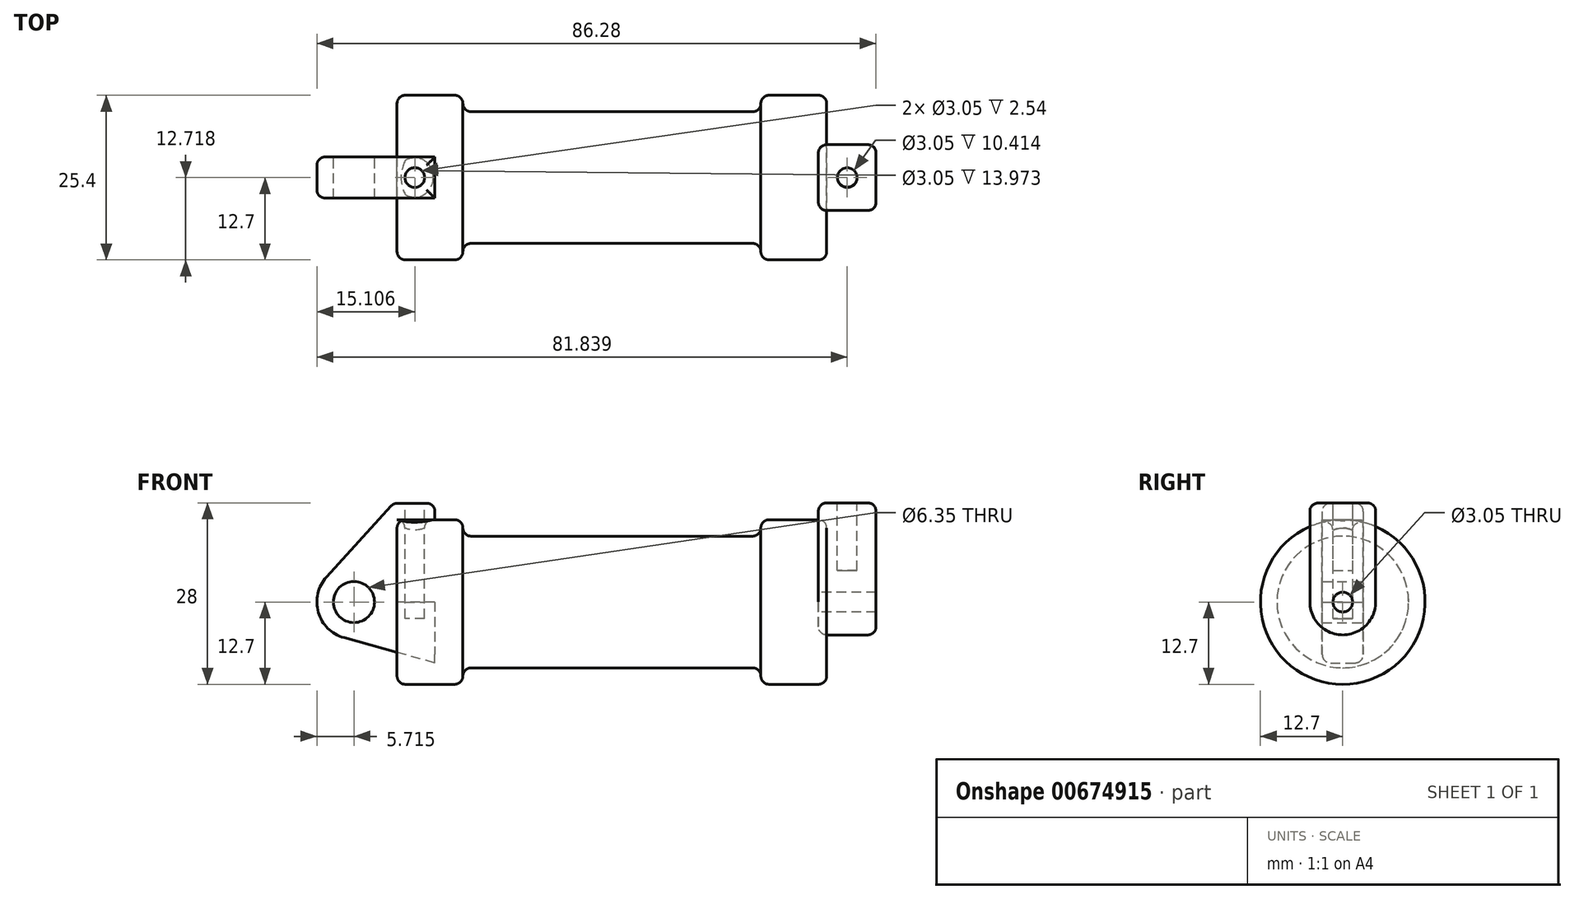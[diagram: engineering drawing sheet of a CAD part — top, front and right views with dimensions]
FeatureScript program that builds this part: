
annotation { "Feature Type Name" : "Feature", "Feature Type Description" : "" }
export const myFeature = defineFeature(function(context is Context, id is Id, definition is map)
    precondition{}
    {
        {
            var Q0;
            Q0=qCreatedBy(makeId("Front.planeOp"),FACE);
            var sketch = newSketch(context, id + "F0", { "sketchPlane" : qUnion([Q0])});
            skLineSegment(sketch, "E0", {"start": v(0, 0) * mm, "end": v(0, 12.7) * mm});
            skLineSegment(sketch, "E1", {"start": v(0, 12.7) * mm, "end": v(10.16, 12.7) * mm});
            skLineSegment(sketch, "E2", {"start": v(10.16, 12.7) * mm, "end": v(10.16, 10.16) * mm});
            skLineSegment(sketch, "E3", {"start": v(10.16, 10.16) * mm, "end": v(56.13, 10.16) * mm});
            skLineSegment(sketch, "E4", {"start": v(56.13, 10.16) * mm, "end": v(56.13, 12.7) * mm});
            skLineSegment(sketch, "E5", {"start": v(56.13, 12.7) * mm, "end": v(66.3, 12.7) * mm});
            skLineSegment(sketch, "E6", {"start": v(66.3, 12.7) * mm, "end": v(66.3, 0) * mm});
            skLineSegment(sketch, "E7", {"start": v(66.3, 0) * mm, "end": v(0, 0) * mm});
            skLineSegment(sketch, "E8", {"start": v(5.84, 15.24) * mm, "end": v(-0.5, 15.24) * mm});
            skLineSegment(sketch, "E9", {"start": v(-0.5, 15.24) * mm, "end": v(-10.88, 3.85) * mm});
            skLineSegment(sketch, "E10", {"start": v(0, 0) * mm, "end": v(-6.65, 0) * mm});
            skCircle(sketch, "E11", {"center": v(-6.65, 0) * mm, "radius": 5.72 * mm});
            skCircle(sketch, "E12", {"center": v(-6.65, 0) * mm, "radius": 3.18 * mm});
            skLineSegment(sketch, "E13", {"start": v(5.84, 15.24) * mm, "end": v(5.84, -9.4) * mm});
            skLineSegment(sketch, "E14", {"start": v(5.84, -9.4) * mm, "end": v(-8.18, -5.5) * mm});
            skSolve(sketch);
        }
        {
            var Q0;
            {var subQ0=sQuery(id+"F0.wireOp",EDGE,"E2");Q0=makeQuery(id+"F0.imprint","IMPRINT",FACE,{"disambiguationData":[TD([[makeQuery(id+"F0.imprint","IMPRINT",EDGE,{"derivedFrom":subQ0}),-1.0]])]});}
            var Q1;
            {var subQ0=sQuery(id+"F0.wireOp",EDGE,"E0");Q1=makeQuery(id+"F0.imprint","IMPRINT",FACE,{"disambiguationData":[TD([[makeQuery(id+"F0.imprint","IMPRINT",EDGE,{"derivedFrom":subQ0}),-1.0]])]});}
            var Q2;
            Q2 = qSketchRegion(id + "Fg4UrmAE8MYNZPA_2", true);
            var Q3;
            Q3=sQuery(id+"F0.wireOp",EDGE,"E7");
            revolve(context, id + "F1", {"entities" : qUnion([Q0, Q1, Q2]), "axis" : qUnion([Q3]), "revolveType" : RevolveType.FULL});
        }
        {
            var Q0;
            {var subQ1=sQuery(id+"F0.wireOp",EDGE,"E0");Q0=makeQuery(id+"F0.imprint","IMPRINT",FACE,{"disambiguationData":[TD([[makeQuery(id+"F0.imprint","IMPRINT",EDGE,{"derivedFrom":subQ1}),1.0]])]});}
            var Q1;
            {var subQ5=sQuery(id+"F0.wireOp",EDGE,"E12");Q1=makeQuery(id+"F0.imprint","IMPRINT",FACE,{"disambiguationData":[TD([[makeQuery(id+"F0.imprint","IMPRINT",EDGE,{"derivedFrom":subQ5}),-1.0]])]});}
            var Q2;
            {var subQ0=sQuery(id+"F0.wireOp",EDGE,"E14");Q2=makeQuery(id+"F0.imprint","IMPRINT",FACE,{"disambiguationData":[TD([[makeQuery(id+"F0.imprint","IMPRINT",EDGE,{"derivedFrom":subQ0}),-1.0]])]});}
            var Q3;
            Q3 = qSketchRegion(id + "Fg4UrmAE8MYNZPA_2", true);
            extrude(context, id + "F2", {"entities" : qUnion([Q0, Q1, Q2, Q3]), "endBound" : BoundingType.SYMMETRIC, "depth" : 6.35 * mm, "offsetDistance" : 25.4 * mm});
        }
        {
            var Q0;
            Q0=makeQuery(id+"F1.opRevolve","SWEPT_FACE",FACE,{"disambiguationData":[OSD([sQuery(id+"F0.wireOp",EDGE,"E6")])]});
            var sketch = newSketch(context, id + "F3", { "sketchPlane" : qUnion([Q0])});
            skCircle(sketch, "E15", {"center": v(0, 0) * mm, "radius": 5.08 * mm});
            skCircle(sketch, "E16", {"center": v(0, 0) * mm, "radius": 1.52 * mm});
            skLineSegment(sketch, "E17", {"start": v(5.08, 0.06) * mm, "end": v(5.08, 15.3) * mm});
            skLineSegment(sketch, "E18", {"start": v(-5.08, 0.03) * mm, "end": v(-5.08, 15.27) * mm});
            skLineSegment(sketch, "E19", {"start": v(-5.08, 15.27) * mm, "end": v(5.08, 15.3) * mm});
            skSolve(sketch);
        }
        {
            var Q0;
            {var subQ0=sQuery(id+"F3.wireOp",EDGE,"E17");var subQ1=sQuery(id+"F3.wireOp",EDGE,"E15");var subQ2=makeQuery(id+"F3.imprint","INTERSECT",VERTEX,{"derivedFrom":[subQ1,subQ0]});Q0=makeQuery(id+"F3.imprint","IMPRINT",FACE,{"disambiguationData":[TD([[makeQuery(id+"F3.imprint","IMPRINT",EDGE,{"disambiguationData":[TD([[subQ2,-1.0]])],"derivedFrom":subQ1}),-1.0]])]});}
            var Q1;
            Q1=makeQuery(id+"F3.imprint","IMPRINT",FACE,{"disambiguationData":[TD([[makeQuery(id+"F3.imprint","IMPRINT",EDGE,{"derivedFrom":sQuery(id+"F3.wireOp",EDGE,"E16")}),-1.0]])]});
            var Q2;
            {var subQ0=sQuery(id+"F3.wireOp",EDGE,"E19");Q2=makeQuery(id+"F3.imprint","IMPRINT",FACE,{"disambiguationData":[TD([[makeQuery(id+"F3.imprint","IMPRINT",EDGE,{"derivedFrom":subQ0}),-1.0]])]});}
            extrude(context, id + "F4", {"entities" : qUnion([Q0, Q1, Q2]), "depth" : 7.62 * mm, "offsetDistance" : 25.4 * mm, "hasSecondDirection" : true, "secondDirectionOppositeDirection" : true, "secondDirectionDepth" : 1.27 * mm});
        }
        {
            var Q0;
            Q0=makeQuery(id+"F2.opExtrude","SWEPT_FACE",FACE,{"disambiguationData":[OSD([sQuery(id+"F0.wireOp",EDGE,"E8")])]});
            var sketch = newSketch(context, id + "F5", { "sketchPlane" : qUnion([Q0])});
            skCircle(sketch, "E20", {"center": v(2.74, 0) * mm, "radius": 1.52 * mm});
            skPoint(sketch, "E21", {"position": v(5.84, 0) * mm});
            skSolve(sketch);
        }
        {
            var Q0;
            Q0=makeQuery(id+"F5.imprint","IMPRINT",FACE,{"disambiguationData":[TD([[makeQuery(id+"F5.imprint","IMPRINT",EDGE,{"derivedFrom":sQuery(id+"F5.wireOp",EDGE,"E20")}),1.0]])]});
            extrude(context, id + "F6", {"entities" : qUnion([Q0]), "operationType" : NewBodyOperationType.REMOVE, "oppositeDirection" : true, "depth" : 17.78 * mm, "offsetDistance" : 25.4 * mm});
        }
        {
            var Q0;
            Q0=makeQuery(id+"F4.opExtrude","SWEPT_FACE",FACE,{"disambiguationData":[OSD([sQuery(id+"F3.wireOp",EDGE,"E19")])]});
            var sketch = newSketch(context, id + "F7", { "sketchPlane" : qUnion([Q0])});
            skCircle(sketch, "E22", {"center": v(69.47, 0.05) * mm, "radius": 1.52 * mm});
            skSolve(sketch);
        }
        {
            var Q0;
            Q0=makeQuery(id+"F7.imprint","IMPRINT",FACE,{"disambiguationData":[TD([[makeQuery(id+"F7.imprint","IMPRINT",EDGE,{"derivedFrom":sQuery(id+"F7.wireOp",EDGE,"E22")}),1.0]])]});
            extrude(context, id + "F8", {"entities" : qUnion([Q0]), "operationType" : NewBodyOperationType.REMOVE, "oppositeDirection" : true, "depth" : 10.4 * mm, "offsetDistance" : 25.4 * mm});
        }
        {
            var Q0;
            Q0=makeQuery(id+"F1.opRevolve","SWEPT_FACE",FACE,{"disambiguationData":[OSD([sQuery(id+"F0.wireOp",EDGE,"E5")])]});
            var Q1;
            Q1=makeQuery(id+"F1.opRevolve","SWEPT_FACE",FACE,{"disambiguationData":[OSD([sQuery(id+"F0.wireOp",EDGE,"E3")])]});
            var Q2;
            Q2=makeQuery(id+"F1.opRevolve","SWEPT_FACE",FACE,{"disambiguationData":[OSD([sQuery(id+"F0.wireOp",EDGE,"E1")])]});
            fillet(context, id + "F9", {"entities" : qUnion([Q0, Q1, Q2]), "radius" : 1.27 * mm, "tangentPropagation" : true, "allowEdgeOverflow" : false});
        }
        {
            var Q0;
            Q0=makeQuery(id+"F4.opExtrude","SWEPT_FACE",FACE,{"disambiguationData":[OSD([sQuery(id+"F3.wireOp",EDGE,"E15")])]});
            var Q1;
            Q1=makeQuery(id+"F4.opExtrude","CAP_EDGE",EDGE,{"disambiguationData":[OSD([sQuery(id+"F3.wireOp",EDGE,"E19")])],"isStart":true});
            var Q2;
            Q2=makeQuery(id+"F4.opExtrude","CAP_EDGE",EDGE,{"disambiguationData":[OSD([sQuery(id+"F3.wireOp",EDGE,"E19")])],"isStart":false});
            var Q3;
            Q3=makeQuery(id+"F4.opExtrude","SWEPT_FACE",FACE,{"disambiguationData":[OSD([sQuery(id+"F3.wireOp",EDGE,"E17")])]});
            var Q4;
            Q4=makeQuery(id+"F1.opRevolve","SWEPT_FACE",FACE,{"disambiguationData":[OSD([sQuery(id+"F0.wireOp",EDGE,"E6")])]});
            fillet(context, id + "F10", {"entities" : qUnion([Q0, Q1, Q2, Q3, Q4]), "radius" : 1.27 * mm, "tangentPropagation" : true, "allowEdgeOverflow" : false});
        }
        {
            var Q0;
            Q0=makeQuery(id+"F2.opExtrude","CAP_EDGE",EDGE,{"disambiguationData":[OSD([sQuery(id+"F0.wireOp",EDGE,"E9")])],"isStart":false});
            var Q1;
            Q1=makeQuery(id+"F2.opExtrude","CAP_EDGE",EDGE,{"disambiguationData":[OSD([sQuery(id+"F0.wireOp",EDGE,"E8")])],"isStart":false});
            var Q2;
            Q2=makeQuery(id+"F2.opExtrude","SWEPT_EDGE",EDGE,{"disambiguationData":[OSD([sQuery(id+"F0.wireOp",EDGE,"E8"),sQuery(id+"F0.wireOp",EDGE,"E13")])]});
            var Q3;
            Q3=makeQuery(id+"F2.opExtrude","CAP_EDGE",EDGE,{"disambiguationData":[OSD([sQuery(id+"F0.wireOp",EDGE,"E8")])],"isStart":true});
            var Q4;
            Q4=makeQuery(id+"F2.opExtrude","SWEPT_EDGE",EDGE,{"disambiguationData":[OSD([sQuery(id+"F0.wireOp",EDGE,"E8"),sQuery(id+"F0.wireOp",EDGE,"E9")])]});
            var Q5;
            Q5=makeQuery(id+"F2.opExtrude","CAP_EDGE",EDGE,{"disambiguationData":[OSD([sQuery(id+"F0.wireOp",EDGE,"E9")])],"isStart":true});
            var Q6;
            Q6=makeQuery(id+"F4.opExtrude","SWEPT_EDGE",EDGE,{"disambiguationData":[OSD([sQuery(id+"F3.wireOp",EDGE,"E18"),sQuery(id+"F3.wireOp",EDGE,"E19")])]});
            fillet(context, id + "F11", {"entities" : qUnion([Q0, Q1, Q2, Q3, Q4, Q5, Q6]), "radius" : 1.27 * mm, "tangentPropagation" : true, "allowEdgeOverflow" : false});
        }
    });
